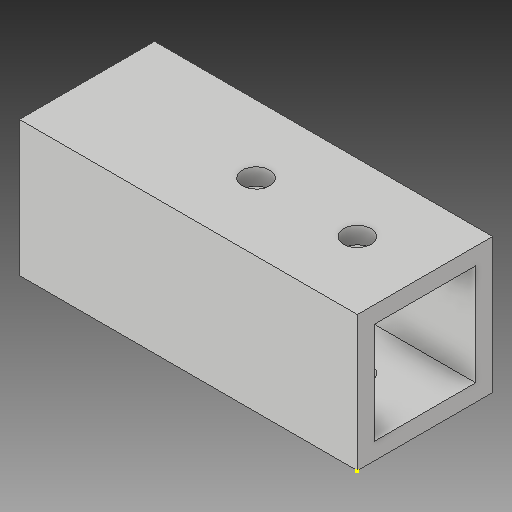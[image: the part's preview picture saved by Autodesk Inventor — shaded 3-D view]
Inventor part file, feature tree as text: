
AUTODESK INVENTOR PART (.ipt)
format: ipt  version: 2018 (Build 220112000, 112)  size: 108,544 bytes
history: native  units: in
note: dims shown in document units (in); Inventor stores cm internally (conversion verified against a paired STEP export)
features: sketch x4, other x3
ambient origin geometry x8: Origin, YZ Plane, XZ Plane, XY Plane, X Axis, Y Axis, Z Axis, Center Point
bodies: Solid1 (feature_tree)
feature tree (7):
  other  "wheel tip connector 1_MIR.ipt"
  other  "Solid1::wheel tip connector 1_MIR.ipt"
  other  "TaggingFeature1"
  sketch  "Sketch1"  dims[d0=0.3937in]
  sketch  "Sketch2"
  sketch  "Sketch3"
  sketch  "Sketch4"
